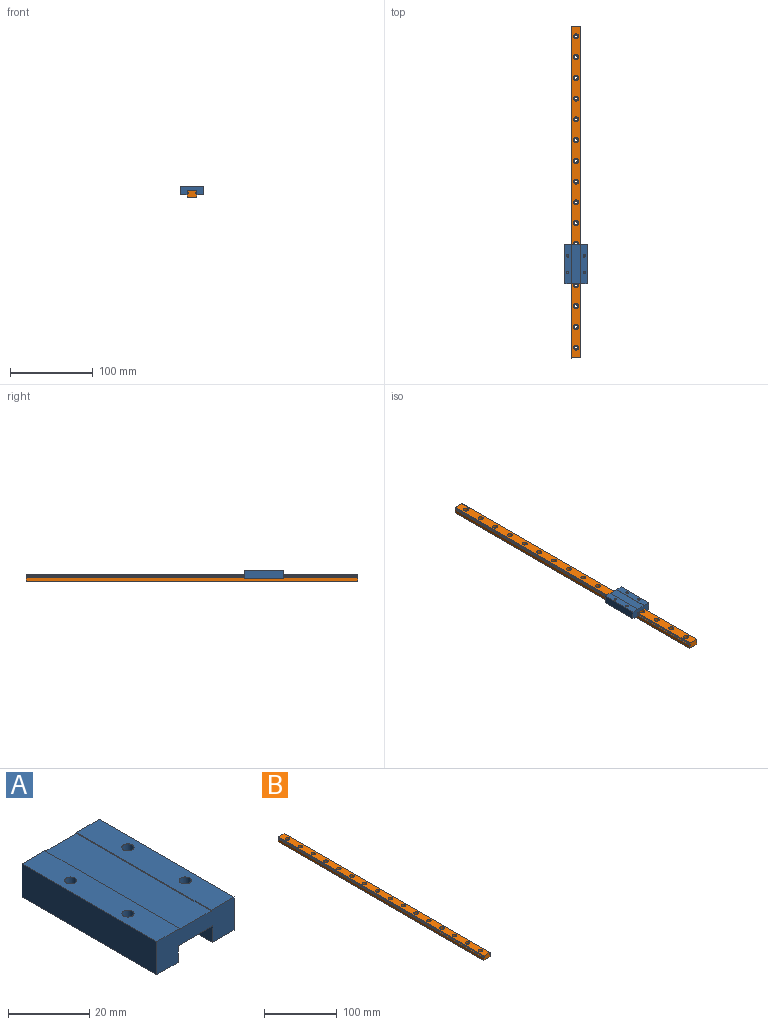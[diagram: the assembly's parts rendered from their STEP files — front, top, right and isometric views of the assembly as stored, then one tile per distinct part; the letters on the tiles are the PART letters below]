
ASSEMBLY  parts=2 mates=1
PART A: 22 faces, bbox 27x47x10 mm
  f0: plane 47x10mm, normal (-1,0,0), area 470mm2, adj f1,f11,f12,f13
  f1: plane 47x7.5mm, normal (0,0,-1), area 352.5mm2, adj f0,f2,f12,f13
  f2: plane 47x5mm, normal (1,0,0), area 235mm2, adj f1,f3,f12,f13
  f3: plane 47x12mm, normal (0,0,-1), area 564mm2, adj f2,f4,f12,f13
  f4: plane 47x5mm, normal (-1,0,0), area 235mm2, adj f3,f5,f12,f13
  f5: plane 47x7.5mm, normal (0,0,-1), area 352.5mm2, adj f4,f6,f12,f13
  f6: plane 47x10mm, normal (1,0,0), area 470mm2, adj f5,f7,f12,f13
  f7: plane 47x8mm, normal (0,0,1), area 361.9mm2, adj f6,f8,f12,f13,f17,f19
  f8: plane 47x0.25mm, normal (-1,0,0), area 11.8mm2, adj f7,f9,f12,f13
  f9: plane 47x11mm, normal (0,0,1), area 517mm2, adj f8,f10,f12,f13
  f10: plane 47x0.25mm, normal (1,0,0), area 11.8mm2, adj f9,f11,f12,f13
  f11: plane 47x8mm, normal (0,0,1), area 361.9mm2, adj f0,f10,f12,f13,f15,f21
  f12: plane 27x10mm, normal (0,-1,0), area 207.2mm2, adj f0,f1,f2,f3,f4,f5,f6,f7
  f13: plane 27x10mm, normal (0,1,0), area 207.2mm2, adj f0,f1,f2,f3,f4,f5,f6,f7
  f14: cone r=0mm half-angle=59deg, axis (0,0,1), area 8.2mm2, adj f15
  f15: cylinder r=1.5mm len=4mm, axis (0,0,1), area 37.7mm2, adj f11,f14
  f16: cone r=0mm half-angle=59deg, axis (0,0,1), area 8.2mm2, adj f17
  f17: cylinder r=1.5mm len=4mm, axis (0,0,1), area 37.7mm2, adj f7,f16
  f18: cone r=0mm half-angle=59deg, axis (0,0,1), area 8.2mm2, adj f19
  f19: cylinder r=1.5mm len=4mm, axis (0,0,1), area 37.7mm2, adj f7,f18
  f20: cone r=0mm half-angle=59deg, axis (0,0,1), area 8.2mm2, adj f21
  f21: cylinder r=1.5mm len=4mm, axis (0,0,1), area 37.7mm2, adj f11,f20
PART B: 68 faces, bbox 12x400x8 mm
  f0: plane 400x4.33mm, normal (1,0,0), area 1733.2mm2, adj f1,f17,f18,f19
  f1: cylinder r=1.12mm len=400mm, axis (0,-1,0), area 427.2mm2, adj f0,f2,f18,f19
  f2: plane 400x0.6mm, normal (0,0,1), area 241.5mm2, adj f1,f3,f18,f19
  f3: plane 400x0.64mm, normal (1,0,0), area 256mm2, adj f2,f4,f18,f19
  f4: plane 400x0.61mm, normal (0,0,-1), area 243.9mm2, adj f3,f5,f18,f19
  f5: cylinder r=1.12mm len=400mm, axis (0,-1,0), area 418.9mm2, adj f4,f6,f18,f19
  f6: plane 400x1.25mm, normal (1,0,0), area 501.2mm2, adj f5,f7,f18,f19
  f7: plane 400x0.3mm, normal (0.71,0,0.71), area 169.7mm2, adj f6,f8,f18,f19
  f8: plane 400x11.4mm, normal (0,0,1), area 4107.6mm2, adj f7,f9,f18,f19,f22,f25,f28,f31
  f9: plane 400x0.3mm, normal (-0.71,0,0.71), area 169.7mm2, adj f8,f10,f18,f19
  f10: plane 400x1.25mm, normal (-1,0,0), area 501.2mm2, adj f9,f11,f18,f19
  f11: cylinder r=1.12mm len=400mm, axis (0,-1,0), area 418.9mm2, adj f10,f12,f18,f19
  f12: plane 400x0.61mm, normal (0,0,-1), area 243.9mm2, adj f11,f13,f18,f19
  f13: plane 400x0.64mm, normal (-1,0,0), area 256mm2, adj f12,f14,f18,f19
  f14: plane 400x0.6mm, normal (0,0,1), area 241.5mm2, adj f13,f15,f18,f19
  f15: cylinder r=1.12mm len=400mm, axis (0,-1,0), area 427.2mm2, adj f14,f16,f18,f19
  f16: plane 400x4.33mm, normal (-1,0,0), area 1733.2mm2, adj f15,f17,f18,f19
  f17: plane 400x12mm, normal (0,0,-1), area 4646.1mm2, adj f0,f16,f18,f19,f20,f23,f26,f29
  f18: plane 12x8mm, normal (0,1,0), area 92.9mm2, adj f0,f1,f2,f3,f4,f5,f6,f7
  f19: plane 12x8mm, normal (0,-1,0), area 92.9mm2, adj f0,f1,f2,f3,f4,f5,f6,f7
  f20: cylinder r=1.75mm len=4mm, axis (0,0,1), area 44mm2, adj f17,f21
  f21: plane 6x6mm, normal (0,0,1), area 18.7mm2, adj f20,f22
  f22: cylinder r=3mm len=6mm, axis (0,0,1), area 75.4mm2, adj f8,f21
  f23: cylinder r=1.75mm len=4mm, axis (0,0,1), area 44mm2, adj f17,f24
  f24: plane 6x6mm, normal (0,0,1), area 18.7mm2, adj f23,f25
  f25: cylinder r=3mm len=6mm, axis (0,0,1), area 75.4mm2, adj f8,f24
  f26: cylinder r=1.75mm len=4mm, axis (0,0,1), area 44mm2, adj f17,f27
  f27: plane 6x6mm, normal (0,0,1), area 18.7mm2, adj f26,f28
  f28: cylinder r=3mm len=6mm, axis (0,0,1), area 75.4mm2, adj f8,f27
  f29: cylinder r=1.75mm len=4mm, axis (0,0,1), area 44mm2, adj f17,f30
  f30: plane 6x6mm, normal (0,0,1), area 18.7mm2, adj f29,f31
  f31: cylinder r=3mm len=6mm, axis (0,0,1), area 75.4mm2, adj f8,f30
  f32: cylinder r=1.75mm len=4mm, axis (0,0,1), area 44mm2, adj f17,f33
  f33: plane 6x6mm, normal (0,0,1), area 18.7mm2, adj f32,f34
  f34: cylinder r=3mm len=6mm, axis (0,0,1), area 75.4mm2, adj f8,f33
  f35: cylinder r=1.75mm len=4mm, axis (0,0,1), area 44mm2, adj f17,f36
  f36: plane 6x6mm, normal (0,0,1), area 18.7mm2, adj f35,f37
  f37: cylinder r=3mm len=6mm, axis (0,0,1), area 75.4mm2, adj f8,f36
  f38: cylinder r=1.75mm len=4mm, axis (0,0,1), area 44mm2, adj f17,f39
  f39: plane 6x6mm, normal (0,0,1), area 18.7mm2, adj f38,f40
  f40: cylinder r=3mm len=6mm, axis (0,0,1), area 75.4mm2, adj f8,f39
  f41: cylinder r=1.75mm len=4mm, axis (0,0,1), area 44mm2, adj f17,f42
  f42: plane 6x6mm, normal (0,0,1), area 18.7mm2, adj f41,f43
  f43: cylinder r=3mm len=6mm, axis (0,0,1), area 75.4mm2, adj f8,f42
  f44: cylinder r=1.75mm len=4mm, axis (0,0,1), area 44mm2, adj f17,f45
  f45: plane 6x6mm, normal (0,0,1), area 18.7mm2, adj f44,f46
  f46: cylinder r=3mm len=6mm, axis (0,0,1), area 75.4mm2, adj f8,f45
  f47: cylinder r=1.75mm len=4mm, axis (0,0,1), area 44mm2, adj f17,f48
  f48: plane 6x6mm, normal (0,0,1), area 18.7mm2, adj f47,f49
  f49: cylinder r=3mm len=6mm, axis (0,0,1), area 75.4mm2, adj f8,f48
  f50: cylinder r=1.75mm len=4mm, axis (0,0,1), area 44mm2, adj f17,f51
  f51: plane 6x6mm, normal (0,0,1), area 18.7mm2, adj f50,f52
  f52: cylinder r=3mm len=6mm, axis (0,0,1), area 75.4mm2, adj f8,f51
  f53: cylinder r=1.75mm len=4mm, axis (0,0,1), area 44mm2, adj f17,f54
  f54: plane 6x6mm, normal (0,0,1), area 18.7mm2, adj f53,f55
  f55: cylinder r=3mm len=6mm, axis (0,0,1), area 75.4mm2, adj f8,f54
  f56: cylinder r=1.75mm len=4mm, axis (0,0,1), area 44mm2, adj f17,f57
  f57: plane 6x6mm, normal (0,0,1), area 18.7mm2, adj f56,f58
  f58: cylinder r=3mm len=6mm, axis (0,0,1), area 75.4mm2, adj f8,f57
  f59: cylinder r=1.75mm len=4mm, axis (0,0,1), area 44mm2, adj f17,f60
  f60: plane 6x6mm, normal (0,0,1), area 18.7mm2, adj f59,f61
  f61: cylinder r=3mm len=6mm, axis (0,0,1), area 75.4mm2, adj f8,f60
  f62: cylinder r=1.75mm len=4mm, axis (0,0,1), area 44mm2, adj f17,f63
  f63: plane 6x6mm, normal (0,0,1), area 18.7mm2, adj f62,f64
  f64: cylinder r=3mm len=6mm, axis (0,0,1), area 75.4mm2, adj f8,f63
  f65: cylinder r=1.75mm len=4mm, axis (0,0,1), area 44mm2, adj f17,f66
  f66: plane 6x6mm, normal (0,0,1), area 18.7mm2, adj f65,f67
  f67: cylinder r=3mm len=6mm, axis (0,0,1), area 75.4mm2, adj f8,f66
PLACE A t=(-44.89,57.25,38.54)mm
PLACE B t=(-44.89,-55.74,35.54)mm fixed
MATE slider B.f19 <-> A.f12  axis (0,-1,0) through (-44.89,-55.74,38.54)mm
